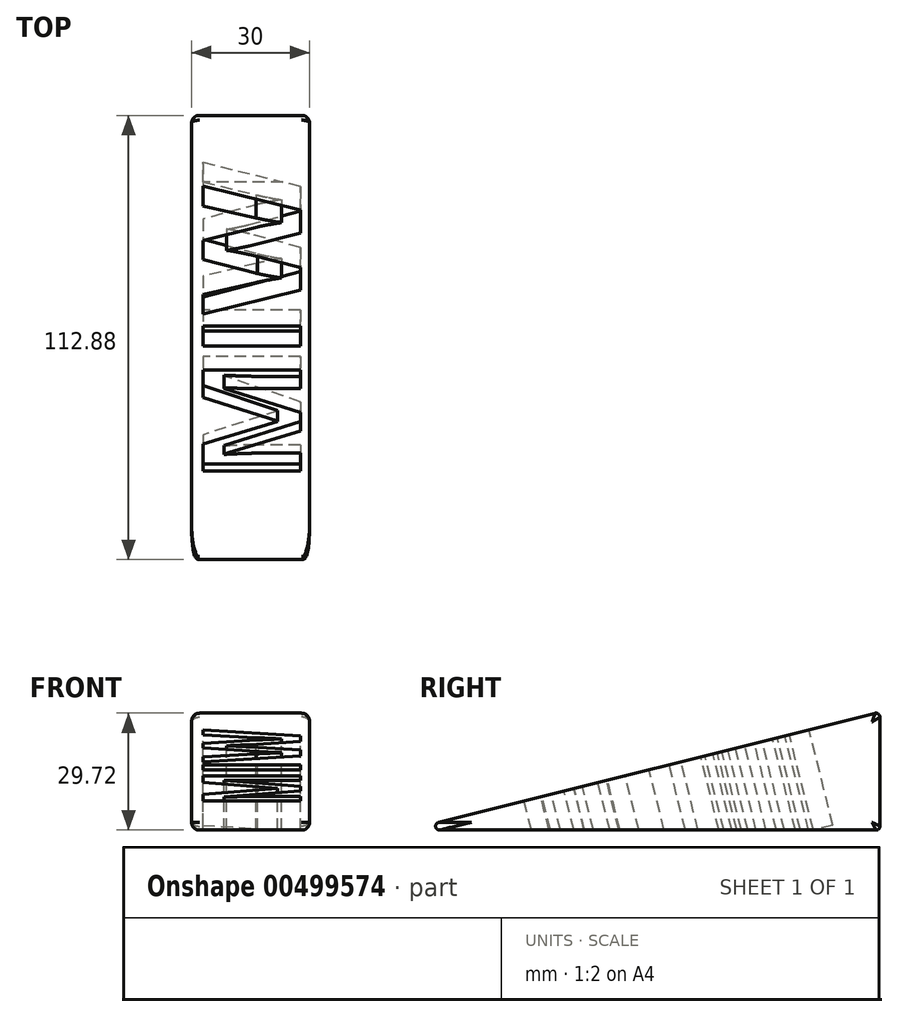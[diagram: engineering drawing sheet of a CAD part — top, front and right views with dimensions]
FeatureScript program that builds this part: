
annotation { "Feature Type Name" : "Feature", "Feature Type Description" : "" }
export const myFeature = defineFeature(function(context is Context, id is Id, definition is map)
    precondition{}
    {
        {
            var Q0;
            Q0=qCreatedBy(makeId("Right.planeOp"),FACE);
            var sketch = newSketch(context, id + "F0", { "sketchPlane" : qUnion([Q0])});
            skLineSegment(sketch, "E0", {"start": v(0, 0) * mm, "end": v(59, 0) * mm});
            skLineSegment(sketch, "E1", {"start": v(0, 0) * mm, "end": v(-51.88, 0) * mm});
            skLineSegment(sketch, "E2", {"start": v(60, 1) * mm, "end": v(60, 28.72) * mm});
            skLineSegment(sketch, "E3", {"start": v(58.76, 29.69) * mm, "end": v(-52.12, 1.97) * mm});
            skPoint(sketch, "E4.visualSharp", {"position": v(60, 30) * mm});
            skArc(sketch, "E4.filletArc", {"start": v(60, 28.72) * mm, "mid": v(59.62, 29.5) * mm, "end": v(58.76, 29.69) * mm});
            skPoint(sketch, "E5.visualSharp", {"position": v(60, 0) * mm});
            skArc(sketch, "E5.filletArc", {"start": v(59, 0) * mm, "mid": v(59.7, 0.3) * mm, "end": v(60, 1) * mm});
            skPoint(sketch, "E6.visualSharp", {"position": v(-60, 0) * mm});
            skArc(sketch, "E6.filletArc", {"start": v(-52.12, 1.97) * mm, "mid": v(-52.87, 0.88) * mm, "end": v(-51.88, 0) * mm});
            skSolve(sketch);
        }
        {
            var Q0;
            Q0=makeQuery(id+"F0.imprint","IMPRINT",FACE,{"disambiguationData":[TD([[makeQuery(id+"F0.imprint","IMPRINT",EDGE,{"derivedFrom":sQuery(id+"F0.wireOp",EDGE,"E0")}),1.0]])]});
            extrude(context, id + "F1", {"entities" : qUnion([Q0]), "depth" : 30 * mm, "symmetric" : true});
        }
        {
            var Q0;
            Q0=makeQuery(id+"F1.opExtrude","SWEPT_FACE",FACE,{"disambiguationData":[OSD([sQuery(id+"F0.wireOp",EDGE,"E3")])]});
            var sketch = newSketch(context, id + "F2", { "sketchPlane" : qUnion([Q0])});
            skText(sketch, "E7", { "text": "MIW", "fontName": "OpenSans-Bold.ttf"});
            const initialGuessF2  = {"E7": [0.01268, -0.0308, 0, 1, 0.02498]};
            skSetInitialGuess(sketch, initialGuessF2);
            skSolve(sketch);
        }
        {
            var Q0;
            Q0 = qSketchRegion(id + "F2", true);
            extrude(context, id + "F3", {"entities" : qUnion([Q0]), "operationType" : NewBodyOperationType.REMOVE, "oppositeDirection" : true, "depth" : 25 * mm});
        }
        {
            var Q0;
            Q0=makeQuery(id+"F1.opExtrude","CAP_EDGE",EDGE,{"disambiguationData":[OSD([sQuery(id+"F0.wireOp",EDGE,"E3")])],"isStart":false});
            var Q1;
            Q1=makeQuery(id+"F1.opExtrude","CAP_EDGE",EDGE,{"disambiguationData":[OSD([sQuery(id+"F0.wireOp",EDGE,"E3")])],"isStart":true});
            fillet(context, id + "F4", {"entities" : qUnion([Q0, Q1]), "radius" : 2 * mm, "tangentPropagation" : true, "allowEdgeOverflow" : false});
        }
    });
